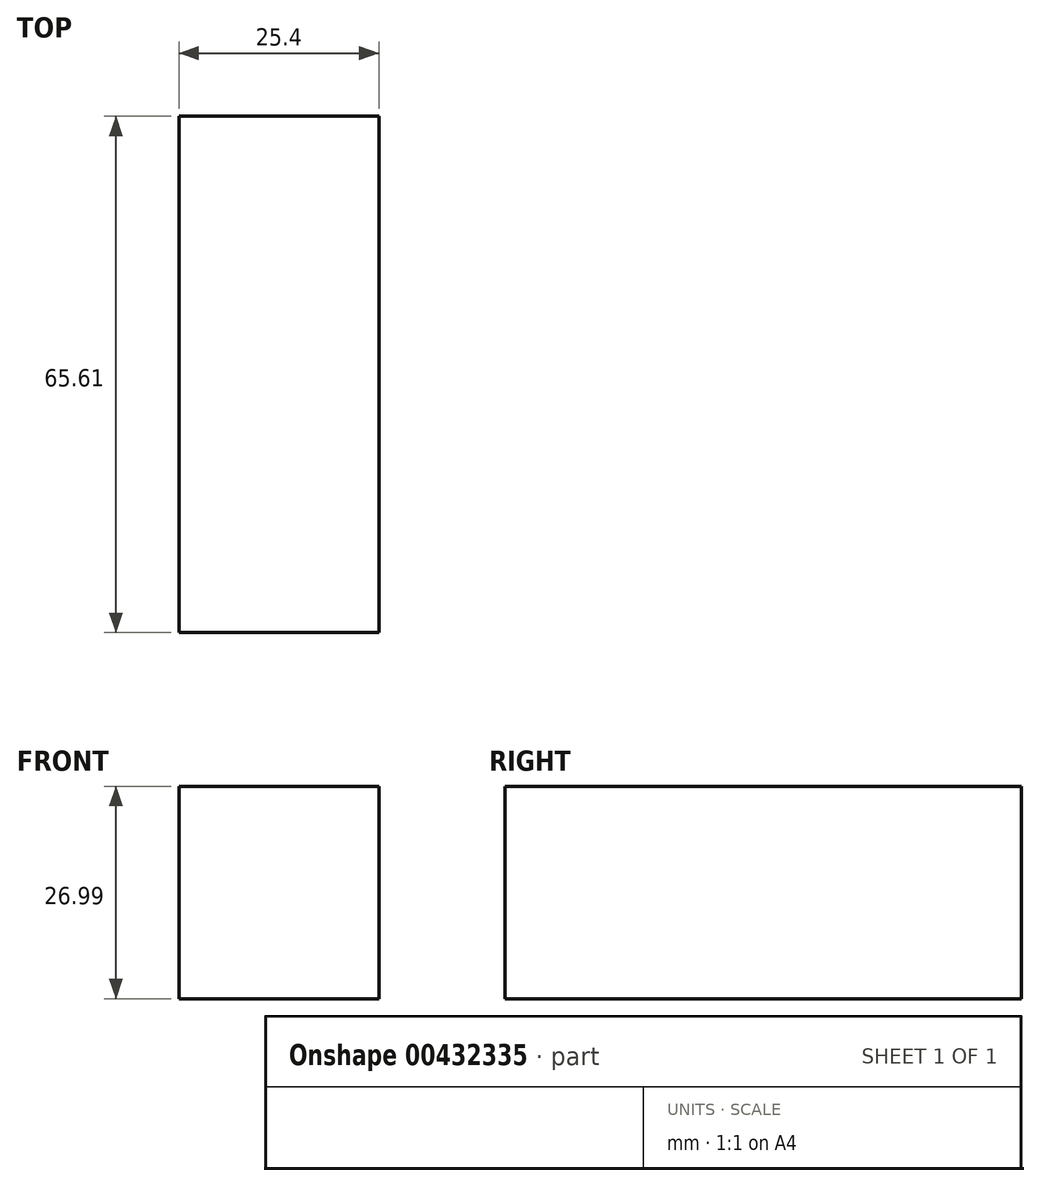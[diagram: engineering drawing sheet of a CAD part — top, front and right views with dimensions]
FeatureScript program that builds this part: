
annotation { "Feature Type Name" : "Feature", "Feature Type Description" : "" }
export const myFeature = defineFeature(function(context is Context, id is Id, definition is map)
    precondition{}
    {
        {
            var Q0;
            Q0=qCreatedBy(makeId("Right.planeOp"),FACE);
            var sketch = newSketch(context, id + "F0", { "sketchPlane" : qUnion([Q0])});
            skLineSegment(sketch, "E0.bottom", {"start": v(0, 0) * mm, "end": v(65.6, 0) * mm});
            skLineSegment(sketch, "E0.top", {"start": v(0, 26.99) * mm, "end": v(65.6, 26.99) * mm});
            skLineSegment(sketch, "E0.left", {"start": v(0, 0) * mm, "end": v(0, 26.99) * mm});
            skLineSegment(sketch, "E0.right", {"start": v(65.6, 0) * mm, "end": v(65.6, 26.99) * mm});
            skLineSegment(sketch, "E1.bottom", {"start": v(45.88, 57.88) * mm, "end": v(45.99, 57.88) * mm});
            skLineSegment(sketch, "E1.top", {"start": v(45.88, 58.73) * mm, "end": v(45.99, 58.73) * mm});
            skLineSegment(sketch, "E1.left", {"start": v(45.88, 57.88) * mm, "end": v(45.88, 58.73) * mm});
            skLineSegment(sketch, "E1.right", {"start": v(45.99, 57.88) * mm, "end": v(45.99, 58.73) * mm});
            skSolve(sketch);
        }
        {
            var Q0;
            Q0=makeQuery(id+"F0.imprint","IMPRINT",FACE,{"disambiguationData":[TD([[makeQuery(id+"F0.imprint","IMPRINT",EDGE,{"derivedFrom":sQuery(id+"F0.wireOp",EDGE,"E0.bottom")}),1.0]])]});
            extrude(context, id + "F1", {"entities" : qUnion([Q0]), "depth" : 25.4 * mm});
        }
        {
            var Q0;
            Q0=makeQuery(id+"F1.opExtrude","CAP_FACE",FACE,{"disambiguationData":[OSD([sQuery(id+"F0.wireOp",EDGE,"E0.bottom"),sQuery(id+"F0.wireOp",EDGE,"E0.top"),sQuery(id+"F0.wireOp",EDGE,"E0.left"),sQuery(id+"F0.wireOp",EDGE,"E0.right")])],"isStart":false});
            var sketch = newSketch(context, id + "F2", { "sketchPlane" : qUnion([Q0])});
            skSolve(sketch);
        }
    });
